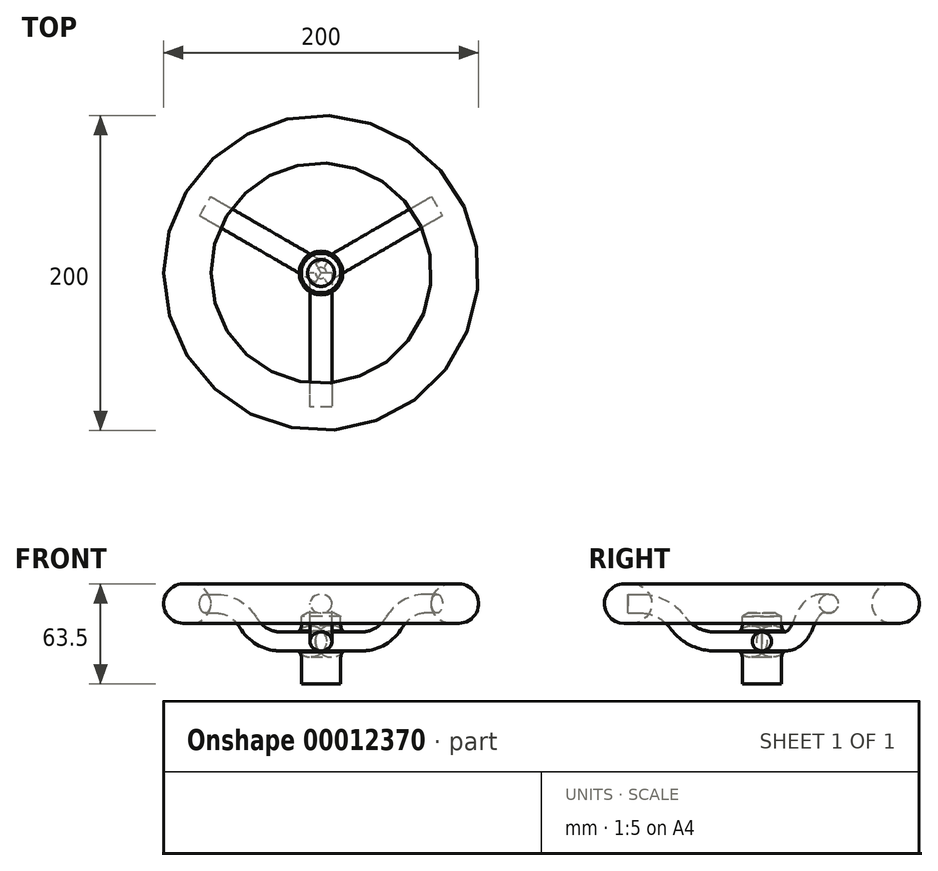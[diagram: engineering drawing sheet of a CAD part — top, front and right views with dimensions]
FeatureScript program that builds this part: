
annotation { "Feature Type Name" : "Feature", "Feature Type Description" : "" }
export const myFeature = defineFeature(function(context is Context, id is Id, definition is map)
    precondition{}
    {
        {
            var Q0;
            Q0=qCreatedBy(makeId("Right.planeOp"),FACE);
            var sketch = newSketch(context, id + "F0", { "sketchPlane" : qUnion([Q0])});
            skLineSegment(sketch, "E0.bottom", {"start": v(0, 0) * mm, "end": v(-12.5, 0) * mm});
            skLineSegment(sketch, "E0.top", {"start": v(0, 45) * mm, "end": v(-12.5, 45) * mm});
            skLineSegment(sketch, "E0.right", {"start": v(-12.5, 0) * mm, "end": v(-12.5, 16.8) * mm});
            skArc(sketch, "E1", {"start": v(-13.83, 33.8) * mm, "mid": v(-16.5, 27) * mm, "end": v(-13.83, 20.2) * mm});
            skLineSegment(sketch, "E2.trimOffspring", {"start": v(-12.5, 37.2) * mm, "end": v(-12.5, 45) * mm});
            skLineSegment(sketch, "E3", {"start": v(0, 45) * mm, "end": v(0, 0) * mm});
            skPoint(sketch, "E4.visualSharp", {"position": v(-12.5, 35) * mm});
            skArc(sketch, "E4.filletArc", {"start": v(-13.83, 33.8) * mm, "mid": v(-12.85, 35.37) * mm, "end": v(-12.5, 37.2) * mm});
            skPoint(sketch, "E5.visualSharp", {"position": v(-12.5, 19) * mm});
            skArc(sketch, "E5.filletArc", {"start": v(-12.5, 16.8) * mm, "mid": v(-12.85, 18.63) * mm, "end": v(-13.83, 20.2) * mm});
            skSolve(sketch);
        }
        {
            var Q0;
            Q0=qSketchRegion(id+"F0",true);
            var Q1;
            Q1=sQuery(id+"F0.wireOp",EDGE,"E3");
            revolve(context, id + "F1", {"entities" : qUnion([Q0]), "axis" : qUnion([Q1]), "revolveType" : RevolveType.FULL});
        }
        {
            var Q0;
            Q0=qCreatedBy(makeId("Right.planeOp"),FACE);
            var sketch = newSketch(context, id + "F2", { "sketchPlane" : qUnion([Q0])});
            skLineSegment(sketch, "E6", {"start": v(0, -13.3) * mm, "end": v(0, 61.57) * mm, "construction": true});
            skSolve(sketch);
        }
        {
            var Q0;
            Q0=qCreatedBy(makeId("Right.planeOp"),FACE);
            var sketch = newSketch(context, id + "F3", { "sketchPlane" : qUnion([Q0])});
            skArc(sketch, "E7", {"start": v(-82.5, 38.5) * mm, "mid": v(-70, 51) * mm, "end": v(-82.5, 63.5) * mm});
            skArc(sketch, "E8.0.MirrorC", {"start": v(-87.5, 38.5) * mm, "mid": v(-100, 51) * mm, "end": v(-87.5, 63.5) * mm});
            skLineSegment(sketch, "E9.bottom", {"start": v(-87.5, 63.5) * mm, "end": v(-82.5, 63.5) * mm});
            skLineSegment(sketch, "E9.top", {"start": v(-87.5, 38.5) * mm, "end": v(-82.5, 38.5) * mm});
            skLineSegment(sketch, "E10", {"start": v(-82.5, 51) * mm, "end": v(-104.34, 51) * mm, "construction": true});
            skLineSegment(sketch, "E11", {"start": v(-85, 63.5) * mm, "end": v(-85, 38.5) * mm, "construction": true});
            skPoint(sketch, "E12.orphan", {"position": v(-70, 51) * mm});
            skPoint(sketch, "E13", {"position": v(0, 0) * mm});
            skPoint(sketch, "E14", {"position": v(-85, 51) * mm});
            skSolve(sketch);
        }
        {
            var Q0;
            Q0=qSketchRegion(id+"F3",true);
            var Q1;
            Q1=sQuery(id+"F2.wireOp",EDGE,"E6");
            revolve(context, id + "F4", {"entities" : qUnion([Q0]), "axis" : qUnion([Q1]), "revolveType" : RevolveType.FULL});
        }
        {
            var Q0;
            Q0=qCreatedBy(makeId("Right.planeOp"),FACE);
            var sketch = newSketch(context, id + "F5", { "sketchPlane" : qUnion([Q0])});
            skLineSegment(sketch, "E15", {"start": v(-76.99, 51) * mm, "end": v(-85, 51) * mm});
            skLineSegment(sketch, "E16", {"start": v(0, 27) * mm, "end": v(-30, 27) * mm});
            skArc(sketch, "E17", {"start": v(-30, 27) * mm, "mid": v(-43.2, 30.17) * mm, "end": v(-53.5, 39) * mm});
            skArc(sketch, "E18", {"start": v(-53.5, 39) * mm, "mid": v(-63.8, 47.83) * mm, "end": v(-76.99, 51) * mm});
            skSolve(sketch);
        }
        {
            var Q0;
            Q0=qCreatedBy(makeId("Front.planeOp"),FACE);
            var sketch = newSketch(context, id + "F6", { "sketchPlane" : qUnion([Q0])});
            skEllipse(sketch, "E19", {"center": v(0, 27) * mm, "majorRadius": 7 * mm, "minorRadius": 6 * mm, "majorAxis": v(1, 0)});
            skSolve(sketch);
        }
        {
            var Q0;
            Q0=makeQuery(id+"F6.imprint","IMPRINT",FACE,{"disambiguationData":[TD([[makeQuery(id+"F6.imprint","IMPRINT",EDGE,{"derivedFrom":sQuery(id+"F6.wireOp",EDGE,"E19")}),1.0]])]});
            var Q1;
            Q1=sQuery(id+"F5.wireOp",EDGE,"E16");
            var Q2;
            Q2=sQuery(id+"F5.wireOp",EDGE,"E17");
            var Q3;
            Q3=sQuery(id+"F5.wireOp",EDGE,"E18");
            var Q4;
            Q4=sQuery(id+"F5.wireOp",EDGE,"E15");
            sweep(context, id + "F7", {"profiles" : qUnion([Q0]), "path" : qUnion([Q1, Q2, Q3, Q4])});
        }
        {
            var Q0;
            Q0=makeQuery(id+"F1.opRevolve","SWEPT_EDGE",EDGE,{"disambiguationData":[OSD([sQuery(id+"F0.wireOp",EDGE,"E0.top"),sQuery(id+"F0.wireOp",EDGE,"E2.trimOffspring")])]});
            chamfer(context, id + "F8", {"entities" : qUnion([Q0]), "chamferType" : ChamferType.TWO_OFFSETS, "width1" : 4 * mm, "oppositeDirection" : false, "width2" : 2 * mm, "tangentPropagation" : true});
        }
        {
            var Q0;
            Q0=makeQuery(id+"F7.opSweep","SWEPT_BODY",BODY,{"disambiguationData":[OSD([sQuery(id+"F5.wireOp",EDGE,"E15"),sQuery(id+"F6.wireOp",EDGE,"E19")])]});
            var Q1;
            Q1=sQuery(id+"F2.wireOp",EDGE,"E6");
            circularPattern(context, id + "F9", {"entities" : qUnion([Q0]), "axis" : qUnion([Q1]), "angle" : 360 * degree, "instanceCount" : round(3), "equalSpace" : true});
        }
    });
